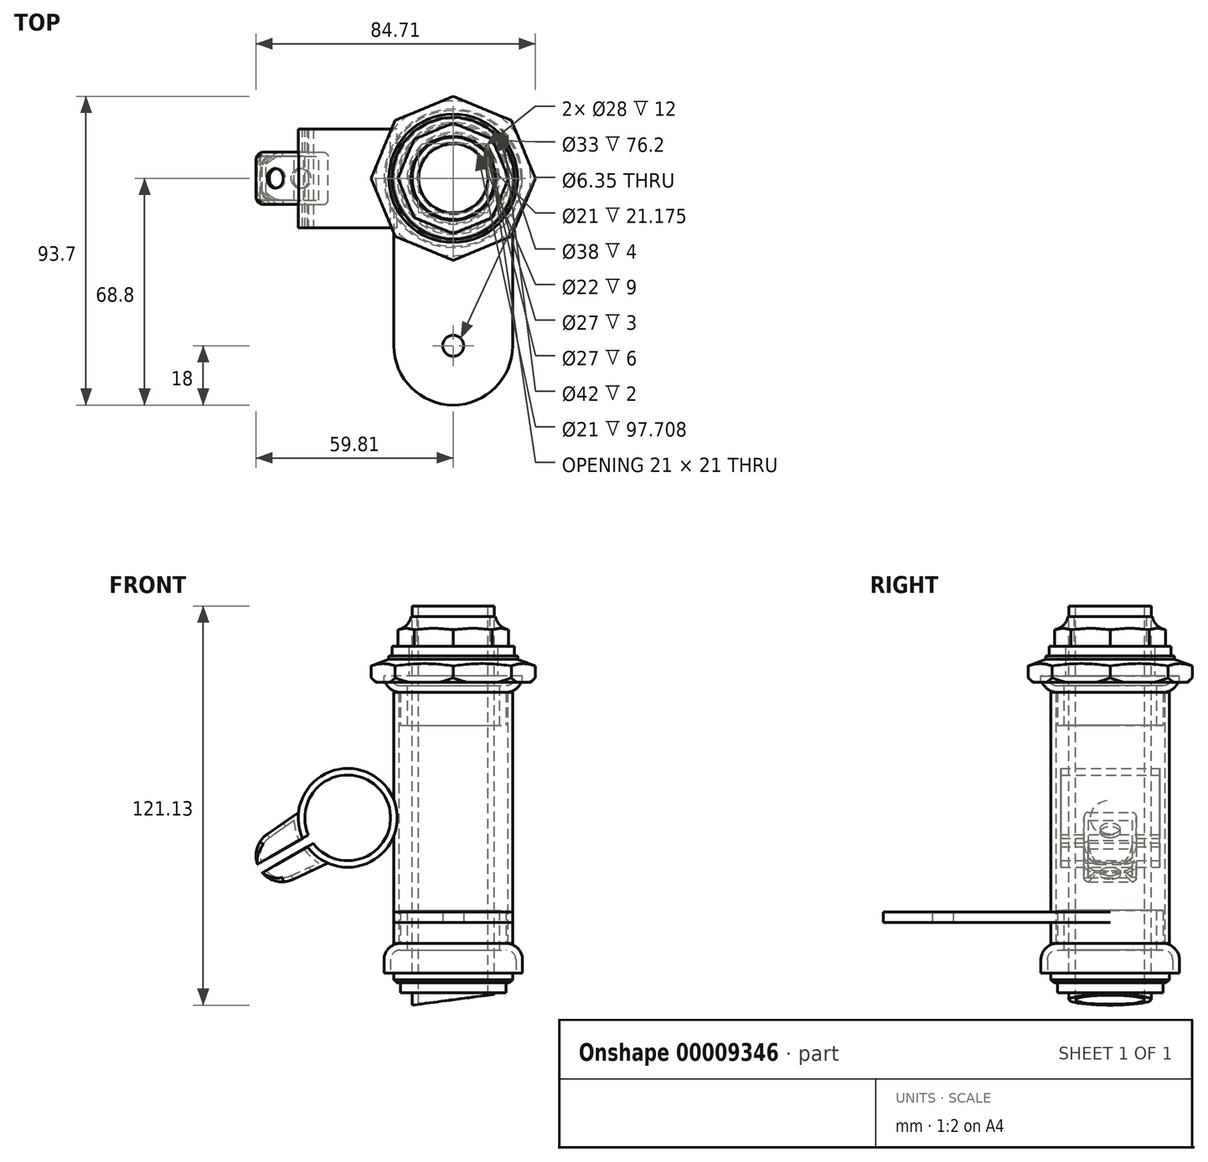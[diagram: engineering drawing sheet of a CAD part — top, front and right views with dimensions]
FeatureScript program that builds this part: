
annotation { "Feature Type Name" : "Feature", "Feature Type Description" : "" }
export const myFeature = defineFeature(function(context is Context, id is Id, definition is map)
    precondition{}
    {
        {
            var Q0;
            Q0=qCreatedBy(makeId("Front.planeOp"),FACE);
            var sketch = newSketch(context, id + "F0", { "sketchPlane" : qUnion([Q0])});
            skLineSegment(sketch, "E0", {"start": v(0, 0) * mm, "end": v(0, 150) * mm, "construction": true});
            skSolve(sketch);
        }
        {
            var Q0;
            Q0=qCreatedBy(makeId("Right.planeOp"),FACE);
            var Q1;
            Q1=sQuery(id+"F0.wireOp",VERTEX,"E0.end");
            cPlane(context, id + "F1", {"entities" : qUnion([Q0, Q1]), "cplaneType" : CPlaneType.PLANE_POINT, "offset" : 150 * mm, "width" : 150 * mm, "height" : 150 * mm});
        }
        {
            var Q0;
            Q0=qCreatedBy(id+"F1.planeOp",FACE);
            var sketch = newSketch(context, id + "F2", { "sketchPlane" : qUnion([Q0])});
            skLineSegment(sketch, "E1", {"start": v(12.5, 150) * mm, "end": v(-12.5, 150) * mm, "construction": true});
            skSolve(sketch);
        }
        {
            var Q0;
            Q0=sQuery(id+"F2.wireOp",EDGE,"E1");
            cPlane(context, id + "F3", {"entities" : qUnion([Q0]), "cplaneType" : CPlaneType.LINE_ANGLE, "offset" : 150 * mm, "angle" : 0 * degree, "width" : 150 * mm, "height" : 150 * mm});
        }
        {
            var Q0;
            Q0=qCreatedBy(id+"F3.planeOp",FACE);
            var sketch = newSketch(context, id + "F4", { "sketchPlane" : qUnion([Q0])});
            skCircle(sketch, "E2", {"center": v(0, 0) * mm, "radius": 12.5 * mm});
            skSolve(sketch);
        }
        {
            var Q0;
            Q0=makeQuery(id+"F4.imprint","IMPRINT",FACE,{"disambiguationData":[TD([[makeQuery(id+"F4.imprint","IMPRINT",EDGE,{"derivedFrom":sQuery(id+"F4.wireOp",EDGE,"E2")}),1.0]])]});
            extrude(context, id + "F5", {"entities" : qUnion([Q0]), "depth" : 173 * mm});
        }
        {
            var Q0;
            Q0=makeQuery(id+"F5.opExtrude","CAP_FACE",FACE,{"disambiguationData":[OSD([sQuery(id+"F4.wireOp",EDGE,"E2")])],"isStart":true});
            var sketch = newSketch(context, id + "F6", { "sketchPlane" : qUnion([Q0])});
            skCircle(sketch, "E3", {"center": v(0, 0) * mm, "radius": 10.5 * mm});
            skSolve(sketch);
        }
        {
            var Q0;
            Q0=qSketchRegion(id+"F6",true);
            extrude(context, id + "F7", {"entities" : qUnion([Q0]), "operationType" : NewBodyOperationType.REMOVE, "endBound" : BoundingType.THROUGH_ALL, "oppositeDirection" : true, "depth" : 25 * mm});
        }
        {
            var Q0;
            Q0=qCreatedBy(makeId("Front.planeOp"),FACE);
            var sketch = newSketch(context, id + "F8", { "sketchPlane" : qUnion([Q0])});
            skLineSegment(sketch, "E4", {"start": v(12.5, 11) * mm, "end": v(16, 11) * mm});
            skLineSegment(sketch, "E5", {"start": v(16, 11) * mm, "end": v(16, 14) * mm});
            skLineSegment(sketch, "E6", {"start": v(16, 14) * mm, "end": v(17, 14) * mm});
            skLineSegment(sketch, "E7", {"start": v(17, 14) * mm, "end": v(18, 15) * mm});
            skLineSegment(sketch, "E8", {"start": v(18, 15) * mm, "end": v(18, 17) * mm});
            skLineSegment(sketch, "E9", {"start": v(18, 17) * mm, "end": v(12.5, 17) * mm});
            skLineSegment(sketch, "E10", {"start": v(12.5, 17) * mm, "end": v(12.5, 11) * mm});
            skLineSegment(sketch, "E11", {"start": v(12.5, 11) * mm, "end": v(12.5, -23) * mm, "construction": true});
            skSolve(sketch);
        }
        {
            var Q0;
            Q0=qSketchRegion(id+"F8",true);
            var Q1;
            Q1=sQuery(id+"F0.wireOp",EDGE,"E0");
            revolve(context, id + "F9", {"operationType" : NewBodyOperationType.ADD, "entities" : qUnion([Q0]), "axis" : qUnion([Q1]), "revolveType" : RevolveType.FULL});
        }
        {
            var Q0;
            Q0=qCreatedBy(makeId("Front.planeOp"),FACE);
            var sketch = newSketch(context, id + "F10", { "sketchPlane" : qUnion([Q0])});
            skLineSegment(sketch, "E12", {"start": v(16, 36) * mm, "end": v(16, 26) * mm});
            skArc(sketch, "E13", {"start": v(21, 21) * mm, "mid": v(19.54, 24.54) * mm, "end": v(16, 26) * mm});
            skLineSegment(sketch, "E14", {"start": v(21, 21) * mm, "end": v(21, 17) * mm});
            skLineSegment(sketch, "E15", {"start": v(16, 26) * mm, "end": v(16, 21) * mm, "construction": true});
            skLineSegment(sketch, "E16", {"start": v(16, 21) * mm, "end": v(21, 21) * mm, "construction": true});
            skLineSegment(sketch, "E17.0", {"start": v(14, 36) * mm, "end": v(14, 24) * mm});
            skLineSegment(sketch, "E18.0", {"start": v(19, 21) * mm, "end": v(19, 17) * mm});
            skArc(sketch, "E19", {"start": v(19, 21) * mm, "mid": v(18.12, 23.12) * mm, "end": v(16, 24) * mm});
            skLineSegment(sketch, "E20", {"start": v(16, 24) * mm, "end": v(14, 24) * mm});
            skLineSegment(sketch, "E21", {"start": v(19, 17) * mm, "end": v(21, 17) * mm});
            skLineSegment(sketch, "E22", {"start": v(14, 36) * mm, "end": v(16, 36) * mm});
            skSolve(sketch);
        }
        {
            var Q0;
            Q0=qSketchRegion(id+"F10",true);
            var Q1;
            Q1=sQuery(id+"F0.wireOp",EDGE,"E0");
            revolve(context, id + "F11", {"entities" : qUnion([Q0]), "axis" : qUnion([Q1]), "revolveType" : RevolveType.FULL});
        }
        {
            var Q0;
            Q0=qCreatedBy(makeId("Front.planeOp"),FACE);
            var sketch = newSketch(context, id + "F12", { "sketchPlane" : qUnion([Q0])});
            skLineSegment(sketch, "E23", {"start": v(16.5, 26) * mm, "end": v(16.5, 102.2) * mm});
            skLineSegment(sketch, "E24", {"start": v(16.5, 102.2) * mm, "end": v(18, 102.2) * mm});
            skLineSegment(sketch, "E25", {"start": v(18, 102.2) * mm, "end": v(18, 26) * mm});
            skLineSegment(sketch, "E26", {"start": v(18, 26) * mm, "end": v(16.5, 26) * mm});
            skSolve(sketch);
        }
        {
            var Q0;
            Q0=qSketchRegion(id+"F12",true);
            var Q1;
            Q1=sQuery(id+"F0.wireOp",EDGE,"E0");
            revolve(context, id + "F13", {"entities" : qUnion([Q0]), "axis" : qUnion([Q1]), "revolveType" : RevolveType.FULL});
        }
        {
            var Q0;
            Q0=qCreatedBy(makeId("Front.planeOp"),FACE);
            var sketch = newSketch(context, id + "F14", { "sketchPlane" : qUnion([Q0])});
            skLineSegment(sketch, "E27", {"start": v(16, 92.2) * mm, "end": v(16, 102.2) * mm});
            skArc(sketch, "E28", {"start": v(16, 102.2) * mm, "mid": v(19.54, 103.66) * mm, "end": v(21, 107.2) * mm});
            skLineSegment(sketch, "E29", {"start": v(16, 107.2) * mm, "end": v(16, 102.2) * mm, "construction": true});
            skLineSegment(sketch, "E30", {"start": v(16, 107.2) * mm, "end": v(19, 107.2) * mm, "construction": true});
            skLineSegment(sketch, "E31", {"start": v(16, 92.2) * mm, "end": v(14, 92.2) * mm});
            skLineSegment(sketch, "E32", {"start": v(14, 92.2) * mm, "end": v(14, 104.2) * mm});
            skArc(sketch, "E33", {"start": v(16, 104.2) * mm, "mid": v(18.12, 105.08) * mm, "end": v(19, 107.2) * mm});
            skLineSegment(sketch, "E34", {"start": v(19, 107.2) * mm, "end": v(21, 107.2) * mm});
            skLineSegment(sketch, "E35", {"start": v(14, 104.2) * mm, "end": v(16, 104.2) * mm});
            skSolve(sketch);
        }
        {
            var Q0;
            Q0=qSketchRegion(id+"F14",true);
            var Q1;
            Q1=sQuery(id+"F0.wireOp",EDGE,"E0");
            revolve(context, id + "F15", {"entities" : qUnion([Q0]), "axis" : qUnion([Q1]), "revolveType" : RevolveType.FULL});
        }
        {
            var Q0;
            Q0=makeQuery(id+"F15.opRevolve","SWEPT_FACE",FACE,{"disambiguationData":[OSD([sQuery(id+"F14.wireOp",EDGE,"E34")])]});
            var sketch = newSketch(context, id + "F16", { "sketchPlane" : qUnion([Q0])});
            skCircle(sketch, "E36", {"center": v(0, 0) * mm, "radius": 13.5 * mm});
            skCircle(sketch, "E37.cCircle", {"center": v(0, 0) * mm, "radius": 23 * mm, "construction": true});
            skLineSegment(sketch, "E37.0", {"start": v(17.6, 17.6) * mm, "end": v(24.9, 0) * mm});
            skLineSegment(sketch, "E37.1", {"start": v(24.9, 0) * mm, "end": v(17.6, -17.6) * mm});
            skLineSegment(sketch, "E37.2", {"start": v(17.6, -17.6) * mm, "end": v(0, -24.9) * mm});
            skLineSegment(sketch, "E37.3", {"start": v(0, -24.9) * mm, "end": v(-17.6, -17.6) * mm});
            skLineSegment(sketch, "E37.4", {"start": v(-17.6, -17.6) * mm, "end": v(-24.9, 0) * mm});
            skLineSegment(sketch, "E37.5", {"start": v(-24.9, 0) * mm, "end": v(-17.6, 17.6) * mm});
            skLineSegment(sketch, "E37.6", {"start": v(-17.6, 17.6) * mm, "end": v(0, 24.9) * mm});
            skLineSegment(sketch, "E37.7", {"start": v(0, 24.9) * mm, "end": v(17.6, 17.6) * mm});
            skPoint(sketch, "E37.0.midPoint", {"position": v(21.25, 8.8) * mm});
            skSolve(sketch);
        }
        {
            var Q0;
            Q0=qSketchRegion(id+"F16",true);
            extrude(context, id + "F17", {"entities" : qUnion([Q0]), "depth" : 6 * mm, "hasSecondDirection" : true, "secondDirectionOppositeDirection" : true, "secondDirectionDepth" : 2 * mm});
        }
        {
            var Q0;
            Q0=qCreatedBy(makeId("Front.planeOp"),FACE);
            var sketch = newSketch(context, id + "F18", { "sketchPlane" : qUnion([Q0])});
            skLineSegment(sketch, "E38", {"start": v(0, 107.2) * mm, "end": v(21, 107.2) * mm});
            skLineSegment(sketch, "E39", {"start": v(21, 107.2) * mm, "end": v(21, 105.2) * mm});
            skLineSegment(sketch, "E40", {"start": v(21, 105.2) * mm, "end": v(0, 105.2) * mm});
            skLineSegment(sketch, "E41", {"start": v(0, 105.2) * mm, "end": v(0, 107.2) * mm});
            skSolve(sketch);
        }
        {
            var Q0;
            Q0=qSketchRegion(id+"F18",true);
            var Q1;
            Q1=sQuery(id+"F0.wireOp",EDGE,"E0");
            revolve(context, id + "F19", {"operationType" : NewBodyOperationType.REMOVE, "entities" : qUnion([Q0]), "axis" : qUnion([Q1]), "revolveType" : RevolveType.FULL, "oppositeDirection" : true});
        }
        {
            var Q0;
            Q0=qCreatedBy(makeId("Front.planeOp"),FACE);
            var sketch = newSketch(context, id + "F20", { "sketchPlane" : qUnion([Q0])});
            skLineSegment(sketch, "E42", {"start": v(24.9, 106.61) * mm, "end": v(23.48, 105.2) * mm});
            skLineSegment(sketch, "E43", {"start": v(23.48, 105.2) * mm, "end": v(24.9, 105.2) * mm});
            skLineSegment(sketch, "E44", {"start": v(24.9, 105.2) * mm, "end": v(24.9, 106.61) * mm});
            skSolve(sketch);
        }
        {
            var Q0;
            Q0=qSketchRegion(id+"F20",true);
            var Q1;
            Q1=sQuery(id+"F0.wireOp",EDGE,"E0");
            revolve(context, id + "F21", {"operationType" : NewBodyOperationType.REMOVE, "entities" : qUnion([Q0]), "axis" : qUnion([Q1]), "revolveType" : RevolveType.FULL, "oppositeDirection" : true});
        }
        {
            var Q0;
            Q0=qCreatedBy(makeId("Front.planeOp"),FACE);
            var sketch = newSketch(context, id + "F22", { "sketchPlane" : qUnion([Q0])});
            skLineSegment(sketch, "E45", {"start": v(19.5, 113.2) * mm, "end": v(19.5, 112.2) * mm});
            skLineSegment(sketch, "E46", {"start": v(19.5, 112.2) * mm, "end": v(24.9, 110.2) * mm});
            skLineSegment(sketch, "E47", {"start": v(24.9, 110.2) * mm, "end": v(24.9, 113.2) * mm});
            skLineSegment(sketch, "E48", {"start": v(24.9, 113.2) * mm, "end": v(19.5, 113.2) * mm});
            skSolve(sketch);
        }
        {
            var Q0;
            Q0=qSketchRegion(id+"F22",true);
            var Q1;
            Q1=sQuery(id+"F0.wireOp",EDGE,"E0");
            revolve(context, id + "F23", {"operationType" : NewBodyOperationType.REMOVE, "entities" : qUnion([Q0]), "axis" : qUnion([Q1]), "revolveType" : RevolveType.FULL, "oppositeDirection" : true});
        }
        {
            var Q0;
            Q0=makeQuery(id+"F17.opExtrude","CAP_FACE",FACE,{"disambiguationData":[OSD([sQuery(id+"F16.wireOp",EDGE,"E36"),sQuery(id+"F16.wireOp",EDGE,"E37.0"),sQuery(id+"F16.wireOp",EDGE,"E37.1"),sQuery(id+"F16.wireOp",EDGE,"E37.2"),sQuery(id+"F16.wireOp",EDGE,"E37.3"),sQuery(id+"F16.wireOp",EDGE,"E37.4"),sQuery(id+"F16.wireOp",EDGE,"E37.5"),sQuery(id+"F16.wireOp",EDGE,"E37.6"),sQuery(id+"F16.wireOp",EDGE,"E37.7")])],"isStart":false});
            var sketch = newSketch(context, id + "F24", { "sketchPlane" : qUnion([Q0])});
            skCircle(sketch, "E49", {"center": v(0, 0) * mm, "radius": 13.5 * mm});
            skCircle(sketch, "E50", {"center": v(0, 0) * mm, "radius": 18.5 * mm});
            skSolve(sketch);
        }
        {
            var Q0;
            Q0=qSketchRegion(id+"F24",true);
            extrude(context, id + "F25", {"entities" : qUnion([Q0]), "depth" : 3 * mm});
        }
        {
            var Q0;
            Q0=makeQuery(id+"F25.opExtrude","CAP_FACE",FACE,{"disambiguationData":[OSD([sQuery(id+"F24.wireOp",EDGE,"E49"),sQuery(id+"F24.wireOp",EDGE,"E50")])],"isStart":false});
            var sketch = newSketch(context, id + "F26", { "sketchPlane" : qUnion([Q0])});
            skCircle(sketch, "E51.cCircle", {"center": v(0, 0) * mm, "radius": 15.5 * mm, "construction": true});
            skLineSegment(sketch, "E51.0", {"start": v(16.78, 0) * mm, "end": v(11.86, -11.86) * mm});
            skLineSegment(sketch, "E51.1", {"start": v(11.86, -11.86) * mm, "end": v(0, -16.78) * mm});
            skLineSegment(sketch, "E51.2", {"start": v(0, -16.78) * mm, "end": v(-11.86, -11.86) * mm});
            skLineSegment(sketch, "E51.3", {"start": v(-11.86, -11.86) * mm, "end": v(-16.78, 0) * mm});
            skLineSegment(sketch, "E51.4", {"start": v(-16.78, 0) * mm, "end": v(-11.86, 11.86) * mm});
            skLineSegment(sketch, "E51.5", {"start": v(-11.86, 11.86) * mm, "end": v(0, 16.78) * mm});
            skLineSegment(sketch, "E51.6", {"start": v(0, 16.78) * mm, "end": v(11.86, 11.86) * mm});
            skLineSegment(sketch, "E51.7", {"start": v(11.86, 11.86) * mm, "end": v(16.78, 0) * mm});
            skPoint(sketch, "E51.0.midPoint", {"position": v(14.32, -5.93) * mm});
            skCircle(sketch, "E52", {"center": v(0, 0) * mm, "radius": 11 * mm});
            skSolve(sketch);
        }
        {
            var Q0;
            Q0=qSketchRegion(id+"F26",true);
            extrude(context, id + "F27", {"entities" : qUnion([Q0]), "depth" : 9 * mm});
        }
        {
            var Q0;
            Q0=qCreatedBy(makeId("Front.planeOp"),FACE);
            var sketch = newSketch(context, id + "F28", { "sketchPlane" : qUnion([Q0])});
            skLineSegment(sketch, "E53", {"start": v(12.78, 125.2) * mm, "end": v(16.78, 125.2) * mm});
            skLineSegment(sketch, "E54", {"start": v(16.78, 125.2) * mm, "end": v(16.78, 121.2) * mm});
            skArc(sketch, "E55", {"start": v(12.78, 125.2) * mm, "mid": v(14.16, 122.58) * mm, "end": v(16.78, 121.2) * mm});
            skLineSegment(sketch, "E56", {"start": v(16.78, 121.2) * mm, "end": v(16.78, 116.2) * mm, "construction": true});
            skLineSegment(sketch, "E57", {"start": v(12.78, 125.2) * mm, "end": v(11, 125.2) * mm, "construction": true});
            skSolve(sketch);
        }
        {
            var Q0;
            Q0=qSketchRegion(id+"F28",true);
            var Q1;
            Q1=sQuery(id+"F0.wireOp",EDGE,"E0");
            revolve(context, id + "F29", {"operationType" : NewBodyOperationType.REMOVE, "entities" : qUnion([Q0]), "axis" : qUnion([Q1]), "revolveType" : RevolveType.FULL, "oppositeDirection" : true});
        }
        {
            var Q0;
            Q0=qCreatedBy(makeId("Front.planeOp"),FACE);
            var sketch = newSketch(context, id + "F30", { "sketchPlane" : qUnion([Q0])});
            skLineSegment(sketch, "E58", {"start": v(-16, 11) * mm, "end": v(16, 11) * mm, "construction": true});
            skLineSegment(sketch, "E59", {"start": v(0, 0) * mm, "end": v(-1.45, 11) * mm, "construction": true});
            skLineSegment(sketch, "E60", {"start": v(-1.15, 8.74) * mm, "end": v(16, 11) * mm, "construction": true});
            skSolve(sketch);
        }
        {
            var Q0;
            Q0=qCreatedBy(makeId("Front.planeOp"),FACE);
            var sketch = newSketch(context, id + "F31", { "sketchPlane" : qUnion([Q0])});
            skLineSegment(sketch, "E61", {"start": v(-12.5, 7.25) * mm, "end": v(12.5, 10.54) * mm});
            skLineSegment(sketch, "E62", {"start": v(12.5, 10.54) * mm, "end": v(12.5, -23) * mm});
            skLineSegment(sketch, "E63", {"start": v(12.5, -23) * mm, "end": v(-12.5, -23) * mm});
            skLineSegment(sketch, "E64", {"start": v(-12.5, -23) * mm, "end": v(-12.5, 7.25) * mm});
            skSolve(sketch);
        }
        {
            var Q0;
            Q0 = qSketchRegion(id + "F31", true);
            extrude(context, id + "F32", {"entities" : qUnion([Q0]), "operationType" : NewBodyOperationType.REMOVE, "endBound" : BoundingType.THROUGH_ALL, "oppositeDirection" : true, "depth" : 25.4 * mm, "hasSecondDirection" : true, "secondDirectionBound" : SecondDirectionBoundingType.THROUGH_ALL, "secondDirectionOppositeDirection" : false, "secondDirectionDepth" : 25.4 * mm});
        }
        {
            var Q0;
            Q0=qCreatedBy(makeId("Front.planeOp"),FACE);
            var sketch = newSketch(context, id + "F33", { "sketchPlane" : qUnion([Q0])});
            skLineSegment(sketch, "E65.bottom", {"start": v(-12.5, 150) * mm, "end": v(12.5, 150) * mm});
            skLineSegment(sketch, "E65.top", {"start": v(-12.5, 128.38) * mm, "end": v(12.5, 128.38) * mm});
            skLineSegment(sketch, "E65.left", {"start": v(-12.5, 150) * mm, "end": v(-12.5, 128.38) * mm});
            skLineSegment(sketch, "E65.right", {"start": v(12.5, 150) * mm, "end": v(12.5, 128.38) * mm});
            skSolve(sketch);
        }
        {
            var Q0;
            Q0 = qSketchRegion(id + "F33", true);
            extrude(context, id + "F34", {"entities" : qUnion([Q0]), "operationType" : NewBodyOperationType.REMOVE, "endBound" : BoundingType.THROUGH_ALL, "oppositeDirection" : true, "depth" : 25.4 * mm, "hasSecondDirection" : true, "secondDirectionBound" : SecondDirectionBoundingType.THROUGH_ALL, "secondDirectionOppositeDirection" : false, "secondDirectionDepth" : 25.4 * mm});
        }
        {
            var Q0;
            Q0=qCreatedBy(makeId("Front.planeOp"),FACE);
            var sketch = newSketch(context, id + "F35", { "sketchPlane" : qUnion([Q0])});
            skCircle(sketch, "E66", {"center": v(-32, 64.1) * mm, "radius": 15 * mm});
            skCircle(sketch, "E67", {"center": v(-32, 64.1) * mm, "radius": 13 * mm});
            skLineSegment(sketch, "E68", {"start": v(-18, 102.2) * mm, "end": v(-18, 26) * mm, "construction": true});
            skLineSegment(sketch, "E69", {"start": v(-18, 64.1) * mm, "end": v(-32, 64.1) * mm, "construction": true});
            skLineSegment(sketch, "E70", {"start": v(-17, 102.2) * mm, "end": v(-17, 26) * mm, "construction": true});
            skSolve(sketch);
        }
        {
            var Q0;
            Q0 = qSketchRegion(id + "F35", true);
            extrude(context, id + "F36", {"entities" : qUnion([Q0]), "operationType" : NewBodyOperationType.ADD, "depth" : 15 * mm, "hasSecondDirection" : true, "secondDirectionOppositeDirection" : true, "secondDirectionDepth" : 15 * mm});
        }
        {
            var Q0;
            Q0=makeQuery(id+"F36.opExtrude","CAP_FACE",FACE,{"disambiguationData":[OSD([sQuery(id+"F35.wireOp",EDGE,"E66"),sQuery(id+"F35.wireOp",EDGE,"E67")])],"isStart":false});
            var sketch = newSketch(context, id + "F37", { "sketchPlane" : qUnion([Q0])});
            skLineSegment(sketch, "E71", {"start": v(-32, 64.1) * mm, "end": v(-45, 56.6) * mm, "construction": true});
            skLineSegment(sketch, "E72", {"start": v(-32, 64.1) * mm, "end": v(-32, 49.1) * mm, "construction": true});
            skLineSegment(sketch, "E73", {"start": v(-45.68, 57.94) * mm, "end": v(-43.93, 58.94) * mm});
            skLineSegment(sketch, "E74", {"start": v(-44.18, 55.34) * mm, "end": v(-42.43, 56.34) * mm});
            skArc(sketch, "E75", {"start": v(-43.93, 58.94) * mm, "mid": v(-43.26, 57.6) * mm, "end": v(-42.43, 56.34) * mm});
            skArc(sketch, "E76", {"start": v(-45.68, 57.94) * mm, "mid": v(-45, 56.6) * mm, "end": v(-44.18, 55.34) * mm});
            skSolve(sketch);
        }
        {
            var Q0;
            Q0=qCreatedBy(makeId("Front.planeOp"),FACE);
            var sketch = newSketch(context, id + "F38", { "sketchPlane" : qUnion([Q0])});
            skArc(sketch, "E77", {"start": v(-56.43, 59.13) * mm, "mid": v(-58.75, 48.66) * mm, "end": v(-48.52, 45.43) * mm});
            skLineSegment(sketch, "E78", {"start": v(-45, 56.6) * mm, "end": v(-51.88, 52.62) * mm, "construction": true});
            skLineSegment(sketch, "E79", {"start": v(-56.43, 59.13) * mm, "end": v(-46.9, 65.8) * mm});
            skLineSegment(sketch, "E80", {"start": v(-48.52, 45.43) * mm, "end": v(-37.98, 50.34) * mm});
            skArc(sketch, "E81", {"start": v(-46.9, 65.8) * mm, "mid": v(-45, 56.6) * mm, "end": v(-37.98, 50.34) * mm});
            skSolve(sketch);
        }
        {
            var Q0;
            Q0=makeQuery(id+"F38.imprint","IMPRINT",FACE,{"disambiguationData":[TD([[makeQuery(id+"F38.imprint","IMPRINT",EDGE,{"derivedFrom":sQuery(id+"F38.wireOp",EDGE,"E77")}),1.0]])]});
            extrude(context, id + "F39", {"entities" : qUnion([Q0]), "depth" : 7.94 * mm});
        }
        {
            var Q0;
            Q0=sQuery(id+"F37.wireOp",EDGE,"E71");
            cPlane(context, id + "F40", {"entities" : qUnion([Q0]), "cplaneType" : CPlaneType.LINE_ANGLE, "offset" : 152.4 * mm, "angle" : 90 * degree, "width" : 152.4 * mm, "height" : 152.4 * mm});
        }
        {
            var Q0;
            Q0=qCreatedBy(id+"F40.planeOp",FACE);
            var sketch = newSketch(context, id + "F41", { "sketchPlane" : qUnion([Q0])});
            skLineSegment(sketch, "E82", {"start": v(-28.14, 0) * mm, "end": v(-28.14, -7.94) * mm});
            skLineSegment(sketch, "E83", {"start": v(-28.14, -7.94) * mm, "end": v(-21.79, -7.94) * mm});
            skLineSegment(sketch, "E84", {"start": v(-28.14, 0) * mm, "end": v(-26.55, 0) * mm});
            skLineSegment(sketch, "E85", {"start": v(-26.55, 0) * mm, "end": v(-26.55, -3.17) * mm});
            skArc(sketch, "E86", {"start": v(-26.55, -3.17) * mm, "mid": v(-25.16, -6.54) * mm, "end": v(-21.79, -7.94) * mm});
            skSolve(sketch);
        }
        {
            var Q0;
            Q0 = qSketchRegion(id + "F41", true);
            extrude(context, id + "F42", {"entities" : qUnion([Q0]), "operationType" : NewBodyOperationType.REMOVE, "endBound" : BoundingType.THROUGH_ALL, "depth" : 25.4 * mm, "hasSecondDirection" : true, "secondDirectionBound" : SecondDirectionBoundingType.THROUGH_ALL, "secondDirectionOppositeDirection" : true, "secondDirectionDepth" : 25.4 * mm});
        }
        {
            var Q0;
            Q0=makeQuery(id+"F39.opExtrude","CAP_EDGE",EDGE,{"disambiguationData":[OSD([sQuery(id+"F38.wireOp",EDGE,"E80")])],"isStart":false});
            var Q1;
            {var subQ0=sQuery(id+"F38.wireOp",EDGE,"E77");var subQ1=sQuery(id+"F38.wireOp",EDGE,"E80");Q1=makeQuery(id+"F42.boolean.opBoolean","SPLIT",EDGE,{"disambiguationData":[TD([makeQuery(id+"F39.opExtrude","SWEPT_FACE",FACE,{"disambiguationData":[OSD([subQ1])]})])],"derivedFrom":makeQuery(id+"F39.opExtrude","CAP_EDGE",EDGE,{"disambiguationData":[OSD([subQ0])],"isStart":false})});}
            var Q2;
            Q2=makeQuery(id+"F42.boolean.opBoolean","INTERSECT",EDGE,{"disambiguationData":[OD(1.0)],"derivedFrom":[makeQuery(id+"F39.opExtrude","SWEPT_FACE",FACE,{"disambiguationData":[OSD([sQuery(id+"F38.wireOp",EDGE,"E77")])]}),makeQuery(id+"F42.opExtrude","SWEPT_FACE",FACE,{"disambiguationData":[OSD([sQuery(id+"F41.wireOp",EDGE,"E86")])]})]});
            var Q3;
            Q3=makeQuery(id+"F42.boolean.opBoolean","INTERSECT",EDGE,{"disambiguationData":[OD(0.0)],"derivedFrom":[makeQuery(id+"F39.opExtrude","SWEPT_FACE",FACE,{"disambiguationData":[OSD([sQuery(id+"F38.wireOp",EDGE,"E77")])]}),makeQuery(id+"F42.opExtrude","SWEPT_FACE",FACE,{"disambiguationData":[OSD([sQuery(id+"F41.wireOp",EDGE,"E86")])]})]});
            var Q4;
            {var subQ0=sQuery(id+"F38.wireOp",EDGE,"E77");var subQ1=sQuery(id+"F38.wireOp",EDGE,"E79");Q4=makeQuery(id+"F42.boolean.opBoolean","SPLIT",EDGE,{"disambiguationData":[TD([makeQuery(id+"F39.opExtrude","SWEPT_FACE",FACE,{"disambiguationData":[OSD([subQ1])]})])],"derivedFrom":makeQuery(id+"F39.opExtrude","CAP_EDGE",EDGE,{"disambiguationData":[OSD([subQ0])],"isStart":false})});}
            var Q5;
            Q5=makeQuery(id+"F39.opExtrude","CAP_EDGE",EDGE,{"disambiguationData":[OSD([sQuery(id+"F38.wireOp",EDGE,"E79")])],"isStart":false});
            fillet(context, id + "F43", {"entities" : qUnion([Q0, Q1, Q2, Q3, Q4, Q5]), "radius" : 1.27 * mm, "tangentPropagation" : true, "allowEdgeOverflow" : false});
        }
        {
            var Q0;
            Q0=makeQuery(id+"F39.opExtrude","CAP_FACE",FACE,{"disambiguationData":[OSD([sQuery(id+"F38.wireOp",EDGE,"E77"),sQuery(id+"F38.wireOp",EDGE,"E79"),sQuery(id+"F38.wireOp",EDGE,"E80"),sQuery(id+"F38.wireOp",EDGE,"E81")])],"isStart":true});
            shell(context, id + "F44", {"entities" : qUnion([Q0]), "thickness" : 1.27 * mm});
        }
        {
            var Q0;
            Q0=makeQuery(id+"F39.opExtrude","SWEPT_BODY",BODY,{"disambiguationData":[OSD([sQuery(id+"F38.wireOp",EDGE,"E77"),sQuery(id+"F38.wireOp",EDGE,"E79"),sQuery(id+"F38.wireOp",EDGE,"E80"),sQuery(id+"F38.wireOp",EDGE,"E81")])]});
            var Q1;
            Q1=qCreatedBy(makeId("Front.planeOp"),FACE);
            mirror(context, id + "F45", {"operationType" : NewBodyOperationType.ADD, "entities" : qUnion([Q0]), "mirrorPlane" : qUnion([Q1])});
        }
        {
            var Q0;
            {var subQ3=sQuery(id+"F37.wireOp",EDGE,"E73");Q0=makeQuery(id+"F37.imprint","IMPRINT",FACE,{"disambiguationData":[TD([[makeQuery(id+"F37.imprint","IMPRINT",EDGE,{"derivedFrom":subQ3}),1.0]])]});}
            var sketch = newSketch(context, id + "F46", { "sketchPlane" : qUnion([Q0])});
            skLineSegment(sketch, "E87", {"start": v(-43.93, 58.94) * mm, "end": v(-59.5, 49.96) * mm});
            skLineSegment(sketch, "E88", {"start": v(-59.5, 49.96) * mm, "end": v(-58, 47.36) * mm});
            skLineSegment(sketch, "E89", {"start": v(-58, 47.36) * mm, "end": v(-42.43, 56.34) * mm});
            skLineSegment(sketch, "E90", {"start": v(-42.43, 56.34) * mm, "end": v(-43.93, 58.94) * mm});
            skSolve(sketch);
        }
        {
            var Q0;
            Q0 = qSketchRegion(id + "F46", true);
            extrude(context, id + "F47", {"entities" : qUnion([Q0]), "operationType" : NewBodyOperationType.REMOVE, "endBound" : BoundingType.THROUGH_ALL, "oppositeDirection" : true, "depth" : 25.4 * mm});
        }
        {
            var Q0;
            Q0=qCreatedBy(id+"F40.planeOp",FACE);
            var sketch = newSketch(context, id + "F48", { "sketchPlane" : qUnion([Q0])});
            skCircle(sketch, "E91", {"center": v(-16.3, 0) * mm, "radius": 3 * mm});
            skSolve(sketch);
        }
        {
            var Q0;
            Q0 = qSketchRegion(id + "F48", true);
            extrude(context, id + "F49", {"entities" : qUnion([Q0]), "operationType" : NewBodyOperationType.REMOVE, "endBound" : BoundingType.THROUGH_ALL, "depth" : 25.4 * mm, "hasSecondDirection" : true, "secondDirectionBound" : SecondDirectionBoundingType.THROUGH_ALL, "secondDirectionOppositeDirection" : true, "secondDirectionDepth" : 25.4 * mm});
        }
        {
            var Q0;
            Q0=qCreatedBy(makeId("Front.planeOp"),FACE);
            var sketch = newSketch(context, id + "F50", { "sketchPlane" : qUnion([Q0])});
            skLineSegment(sketch, "E92", {"start": v(-32, 64.1) * mm, "end": v(-19.05, 65.23) * mm, "construction": true});
            skLineSegment(sketch, "E93", {"start": v(-32, 64.1) * mm, "end": v(-32, 51.1) * mm, "construction": true});
            skSolve(sketch);
        }
        {
            var Q0;
            Q0=makeQuery(id+"F13.opRevolve","SWEPT_FACE",FACE,{"disambiguationData":[OSD([sQuery(id+"F12.wireOp",EDGE,"E26")])]});
            cPlane(context, id + "F51", {"entities" : qUnion([Q0]), "cplaneType" : CPlaneType.OFFSET, "offset" : 6.35 * mm, "oppositeDirection" : true, "width" : 152.4 * mm, "height" : 152.4 * mm});
        }
        {
            var Q0;
            Q0=qCreatedBy(id+"F51.planeOp",FACE);
            var sketch = newSketch(context, id + "F52", { "sketchPlane" : qUnion([Q0])});
            skLineSegment(sketch, "E94", {"start": v(-18, 0) * mm, "end": v(-18, 50.8) * mm});
            skLineSegment(sketch, "E95", {"start": v(18, 0) * mm, "end": v(18, 50.8) * mm});
            skArc(sketch, "E96", {"start": v(18, 50.8) * mm, "mid": v(0, 68.8) * mm, "end": v(-18, 50.8) * mm});
            skArc(sketch, "E97", {"start": v(18, 0) * mm, "mid": v(0, 18) * mm, "end": v(-18, 0) * mm});
            skLineSegment(sketch, "E98", {"start": v(-18, 18) * mm, "end": v(18, 18) * mm, "construction": true});
            skLineSegment(sketch, "E99", {"start": v(-18, 68.8) * mm, "end": v(18, 68.8) * mm, "construction": true});
            skCircle(sketch, "E100", {"center": v(0, 50.8) * mm, "radius": 3.18 * mm});
            skSolve(sketch);
        }
        {
            var Q0;
            Q0 = qSketchRegion(id + "F52", true);
            extrude(context, id + "F53", {"entities" : qUnion([Q0]), "operationType" : NewBodyOperationType.ADD, "oppositeDirection" : true, "depth" : 3.17 * mm});
        }
    });
